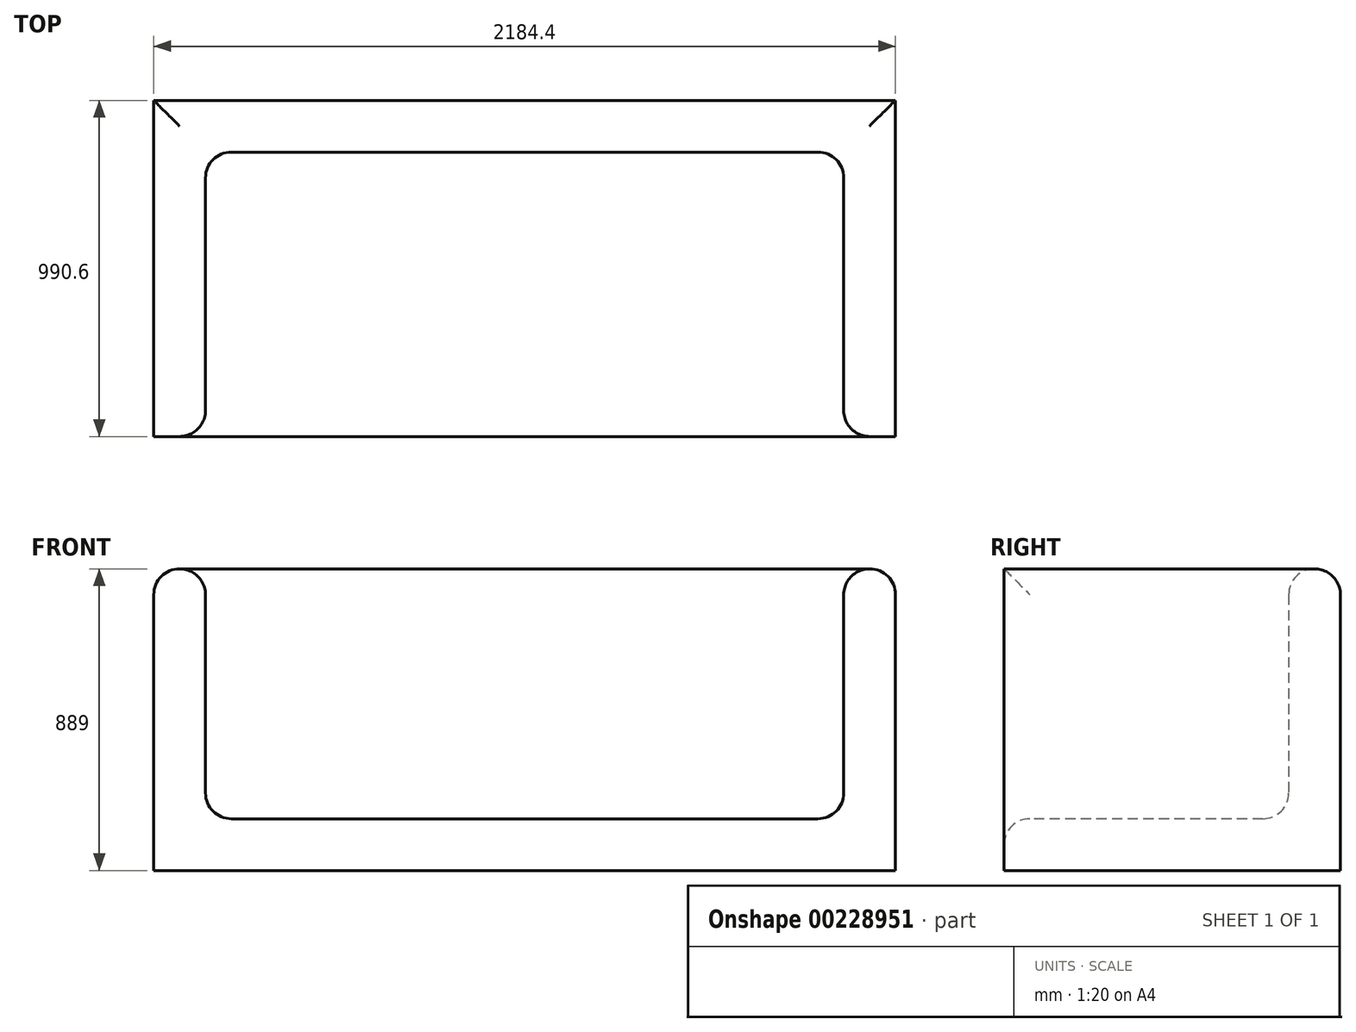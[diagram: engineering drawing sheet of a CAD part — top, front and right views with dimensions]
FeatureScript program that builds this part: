
annotation { "Feature Type Name" : "Feature", "Feature Type Description" : "" }
export const myFeature = defineFeature(function(context is Context, id is Id, definition is map)
    precondition{}
    {
        {
            var Q0;
            Q0=qCreatedBy(makeId("Top.planeOp"),FACE);
            var sketch = newSketch(context, id + "F0", { "sketchPlane" : qUnion([Q0])});
            skLineSegment(sketch, "E0.bottom", {"start": v(-1089.65, 548.63) * mm, "end": v(1094.75, 548.63) * mm});
            skLineSegment(sketch, "E0.top", {"start": v(-1089.65, -441.97) * mm, "end": v(1094.75, -441.97) * mm});
            skLineSegment(sketch, "E0.left", {"start": v(-1089.65, 548.63) * mm, "end": v(-1089.65, -441.97) * mm});
            skLineSegment(sketch, "E0.right", {"start": v(1094.75, 548.63) * mm, "end": v(1094.75, -441.97) * mm});
            skSolve(sketch);
        }
        {
            var Q0;
            Q0=makeQuery(id+"F0.imprint","IMPRINT",FACE,{"disambiguationData":[TD([[makeQuery(id+"F0.imprint","IMPRINT",EDGE,{"derivedFrom":sQuery(id+"F0.wireOp",EDGE,"E0.bottom")}),-1.0]])]});
            extrude(context, id + "F1", {"entities" : qUnion([Q0]), "depth" : 889 * mm});
        }
        {
            var Q0;
            Q0=makeQuery(id+"F1.opExtrude","CAP_FACE",FACE,{"disambiguationData":[OSD([sQuery(id+"F0.wireOp",EDGE,"E0.bottom"),sQuery(id+"F0.wireOp",EDGE,"E0.top"),sQuery(id+"F0.wireOp",EDGE,"E0.left"),sQuery(id+"F0.wireOp",EDGE,"E0.right")])],"isStart":false});
            var Q1;
            Q1=makeQuery(id+"F1.opExtrude","SWEPT_FACE",FACE,{"disambiguationData":[OSD([sQuery(id+"F0.wireOp",EDGE,"E0.top")])]});
            shell(context, id + "F2", {"entities" : qUnion([Q0, Q1]), "thickness" : 152.4 * mm});
        }
        {
            var Q0;
            Q0=makeQuery(id+"F2.opShell","OFFSET_FACE",FACE,{"disambiguationData":[OSD([sQuery(id+"F0.wireOp",EDGE,"E0.bottom")])]});
            var Q1;
            Q1=makeQuery(id+"F2.opShell","OFFSET_FACE",FACE,{"disambiguationData":[OSD([sQuery(id+"F0.wireOp",EDGE,"E0.bottom"),sQuery(id+"F0.wireOp",EDGE,"E0.top"),sQuery(id+"F0.wireOp",EDGE,"E0.left"),sQuery(id+"F0.wireOp",EDGE,"E0.right")])]});
            var Q2;
            Q2=makeQuery(id+"F2.opShell","OFFSET_FACE",FACE,{"disambiguationData":[OSD([sQuery(id+"F0.wireOp",EDGE,"E0.left")])]});
            var Q3;
            Q3=makeQuery(id+"F2.opShell","OFFSET_FACE",FACE,{"disambiguationData":[OSD([sQuery(id+"F0.wireOp",EDGE,"E0.right")])]});
            fillet(context, id + "F3", {"entities" : qUnion([Q0, Q1, Q2, Q3]), "radius" : 76.2 * mm, "tangentPropagation" : true, "allowEdgeOverflow" : false});
        }
        {
            var Q0;
            Q0=makeQuery(id+"F1.opExtrude","CAP_EDGE",EDGE,{"disambiguationData":[OSD([sQuery(id+"F0.wireOp",EDGE,"E0.right")])],"isStart":false});
            var Q1;
            Q1=makeQuery(id+"F1.opExtrude","CAP_EDGE",EDGE,{"disambiguationData":[OSD([sQuery(id+"F0.wireOp",EDGE,"E0.bottom")])],"isStart":false});
            var Q2;
            Q2=makeQuery(id+"F1.opExtrude","CAP_EDGE",EDGE,{"disambiguationData":[OSD([sQuery(id+"F0.wireOp",EDGE,"E0.left")])],"isStart":false});
            fillet(context, id + "F4", {"entities" : qUnion([Q0, Q1, Q2]), "radius" : 76.2 * mm, "tangentPropagation" : true, "allowEdgeOverflow" : false});
        }
    });
